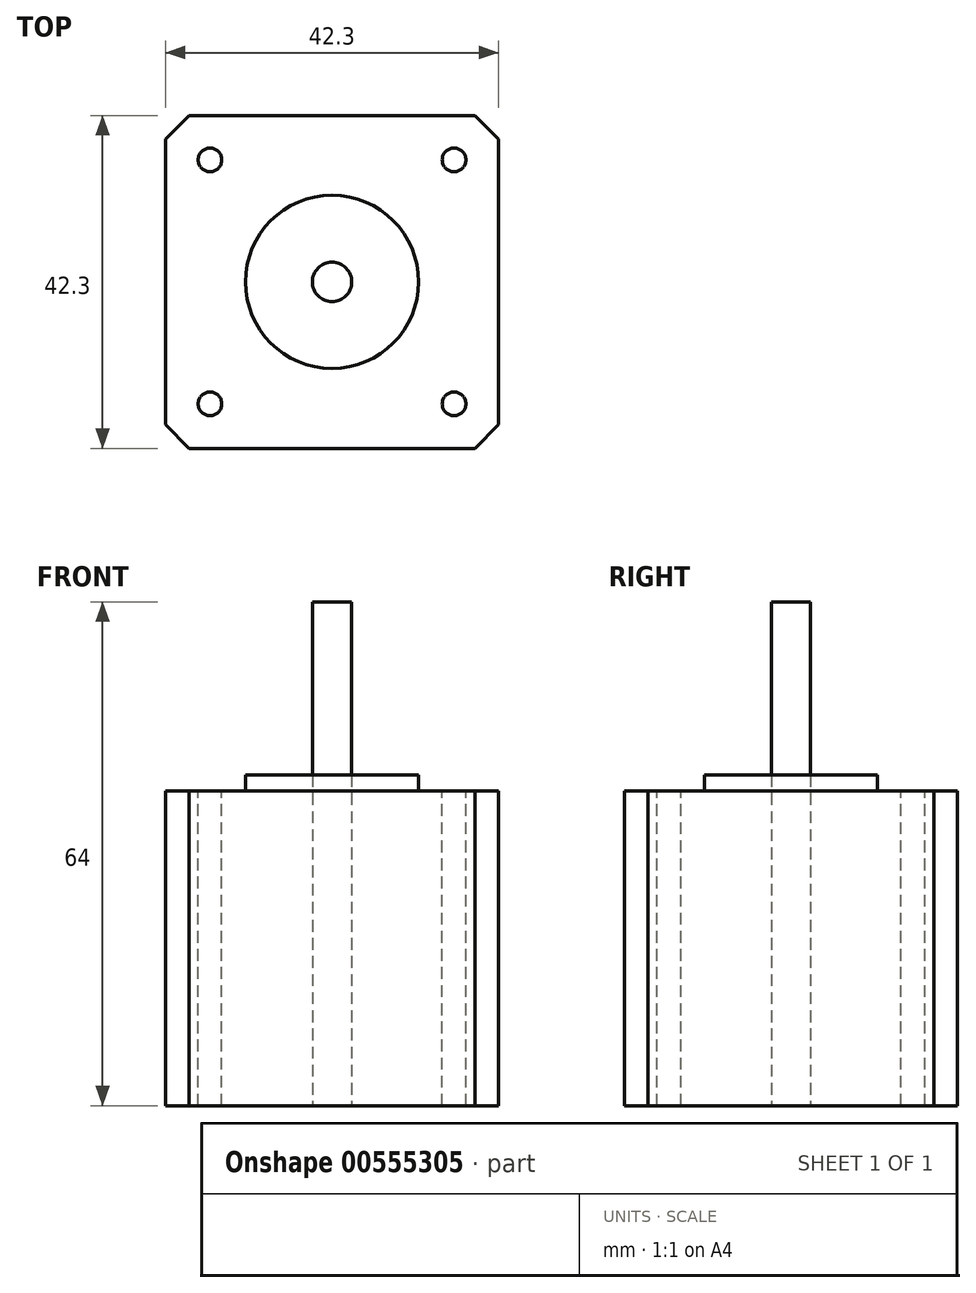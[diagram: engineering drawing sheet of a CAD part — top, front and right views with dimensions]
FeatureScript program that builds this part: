
annotation { "Feature Type Name" : "Feature", "Feature Type Description" : "" }
export const myFeature = defineFeature(function(context is Context, id is Id, definition is map)
    precondition{}
    {
        {
            var Q0;
            Q0=qCreatedBy(makeId("Top.planeOp"),FACE);
            var sketch = newSketch(context, id + "F0", { "sketchPlane" : qUnion([Q0])});
            skLineSegment(sketch, "E0.bottom", {"start": v(21.15, 21.15) * mm, "end": v(-21.15, 21.15) * mm});
            skLineSegment(sketch, "E0.top", {"start": v(21.15, -21.15) * mm, "end": v(-21.15, -21.15) * mm});
            skLineSegment(sketch, "E0.left", {"start": v(21.15, 21.15) * mm, "end": v(21.15, -21.15) * mm});
            skLineSegment(sketch, "E0.right", {"start": v(-21.15, 21.15) * mm, "end": v(-21.15, -21.15) * mm});
            skPoint(sketch, "E0.middle", {"position": v(0, 0) * mm});
            skCircle(sketch, "E1", {"center": v(-15.5, 15.5) * mm, "radius": 1.5 * mm});
            skCircle(sketch, "E2", {"center": v(15.5, 15.5) * mm, "radius": 1.5 * mm});
            skCircle(sketch, "E3", {"center": v(15.5, -15.5) * mm, "radius": 1.5 * mm});
            skCircle(sketch, "E4", {"center": v(-15.5, -15.5) * mm, "radius": 1.5 * mm});
            skCircle(sketch, "E5", {"center": v(0, 0) * mm, "radius": 2.5 * mm});
            skCircle(sketch, "E6", {"center": v(0, 0) * mm, "radius": 11 * mm});
            skSolve(sketch);
        }
        {
            var Q0;
            Q0=makeQuery(id+"F0.imprint","IMPRINT",FACE,{"disambiguationData":[TD([[makeQuery(id+"F0.imprint","IMPRINT",EDGE,{"derivedFrom":sQuery(id+"F0.wireOp",EDGE,"E0.bottom")}),1.0]])]});
            var Q1;
            Q1=makeQuery(id+"F0.imprint","IMPRINT",FACE,{"disambiguationData":[TD([[makeQuery(id+"F0.imprint","IMPRINT",EDGE,{"derivedFrom":sQuery(id+"F0.wireOp",EDGE,"E1")}),1.0]])]});
            var Q2;
            Q2=makeQuery(id+"F0.imprint","IMPRINT",FACE,{"disambiguationData":[TD([[makeQuery(id+"F0.imprint","IMPRINT",EDGE,{"derivedFrom":sQuery(id+"F0.wireOp",EDGE,"E4")}),1.0]])]});
            var Q3;
            Q3=makeQuery(id+"F0.imprint","IMPRINT",FACE,{"disambiguationData":[TD([[makeQuery(id+"F0.imprint","IMPRINT",EDGE,{"derivedFrom":sQuery(id+"F0.wireOp",EDGE,"E3")}),1.0]])]});
            var Q4;
            Q4=makeQuery(id+"F0.imprint","IMPRINT",FACE,{"disambiguationData":[TD([[makeQuery(id+"F0.imprint","IMPRINT",EDGE,{"derivedFrom":sQuery(id+"F0.wireOp",EDGE,"E5")}),-1.0]])]});
            var Q5;
            Q5=makeQuery(id+"F0.imprint","IMPRINT",FACE,{"disambiguationData":[TD([[makeQuery(id+"F0.imprint","IMPRINT",EDGE,{"derivedFrom":sQuery(id+"F0.wireOp",EDGE,"E2")}),1.0]])]});
            extrude(context, id + "F1", {"entities" : qUnion([Q0, Q1, Q2, Q3, Q4, Q5]), "oppositeDirection" : true, "depth" : 40 * mm, "offsetDistance" : 25 * mm});
        }
        {
            var Q0;
            Q0=makeQuery(id+"F0.imprint","IMPRINT",FACE,{"disambiguationData":[TD([[makeQuery(id+"F0.imprint","IMPRINT",EDGE,{"derivedFrom":sQuery(id+"F0.wireOp",EDGE,"E1")}),1.0]])]});
            var Q1;
            Q1=makeQuery(id+"F0.imprint","IMPRINT",FACE,{"disambiguationData":[TD([[makeQuery(id+"F0.imprint","IMPRINT",EDGE,{"derivedFrom":sQuery(id+"F0.wireOp",EDGE,"E4")}),1.0]])]});
            var Q2;
            Q2=makeQuery(id+"F0.imprint","IMPRINT",FACE,{"disambiguationData":[TD([[makeQuery(id+"F0.imprint","IMPRINT",EDGE,{"derivedFrom":sQuery(id+"F0.wireOp",EDGE,"E3")}),1.0]])]});
            var Q3;
            Q3=makeQuery(id+"F0.imprint","IMPRINT",FACE,{"disambiguationData":[TD([[makeQuery(id+"F0.imprint","IMPRINT",EDGE,{"derivedFrom":sQuery(id+"F0.wireOp",EDGE,"E2")}),1.0]])]});
            var Q4;
            Q4=sQuery(id+"F0.wireOp",EDGE,"E4");
            var Q5;
            Q5=sQuery(id+"F0.wireOp",EDGE,"E3");
            var Q6;
            Q6=sQuery(id+"F0.wireOp",EDGE,"E2");
            var Q7;
            Q7=sQuery(id+"F0.wireOp",EDGE,"E1");
            extrude(context, id + "F2", {"entities" : qUnion([Q0, Q1, Q2, Q3]), "operationType" : NewBodyOperationType.REMOVE, "surfaceEntities" : qUnion([Q4, Q5, Q6, Q7]), "oppositeDirection" : true, "depth" : 40 * mm, "offsetDistance" : 25 * mm});
        }
        {
            var Q0;
            Q0=makeQuery(id+"F0.imprint","IMPRINT",FACE,{"disambiguationData":[TD([[makeQuery(id+"F0.imprint","IMPRINT",EDGE,{"derivedFrom":sQuery(id+"F0.wireOp",EDGE,"E5")}),-1.0]])]});
            extrude(context, id + "F3", {"entities" : qUnion([Q0]), "operationType" : NewBodyOperationType.ADD, "depth" : 2 * mm, "offsetDistance" : 25 * mm});
        }
        {
            var Q0;
            Q0=qCreatedBy(makeId("Top.planeOp"),FACE);
            var sketch = newSketch(context, id + "F4", { "sketchPlane" : qUnion([Q0])});
            skCircle(sketch, "E7", {"center": v(0, 0) * mm, "radius": 2.5 * mm});
            skSolve(sketch);
        }
        {
            var Q0;
            Q0=qSketchRegion(id+"F4",true);
            extrude(context, id + "F5", {"entities" : qUnion([Q0]), "depth" : 24 * mm, "offsetDistance" : 25 * mm, "hasSecondDirection" : true, "secondDirectionOppositeDirection" : true, "secondDirectionDepth" : 40 * mm});
        }
        {
            var Q0;
            Q0=makeQuery(id+"F1.opExtrude","SWEPT_EDGE",EDGE,{"disambiguationData":[OSD([sQuery(id+"F0.wireOp",EDGE,"E0.top"),sQuery(id+"F0.wireOp",EDGE,"E0.left")])]});
            var Q1;
            Q1=makeQuery(id+"F1.opExtrude","SWEPT_EDGE",EDGE,{"disambiguationData":[OSD([sQuery(id+"F0.wireOp",EDGE,"E0.bottom"),sQuery(id+"F0.wireOp",EDGE,"E0.left")])]});
            var Q2;
            Q2=makeQuery(id+"F1.opExtrude","SWEPT_EDGE",EDGE,{"disambiguationData":[OSD([sQuery(id+"F0.wireOp",EDGE,"E0.top"),sQuery(id+"F0.wireOp",EDGE,"E0.right")])]});
            var Q3;
            Q3=makeQuery(id+"F1.opExtrude","SWEPT_EDGE",EDGE,{"disambiguationData":[OSD([sQuery(id+"F0.wireOp",EDGE,"E0.bottom"),sQuery(id+"F0.wireOp",EDGE,"E0.right")])]});
            chamfer(context, id + "F6", {"entities" : qUnion([Q0, Q1, Q2, Q3]), "width" : 3 * mm, "tangentPropagation" : true});
        }
    });
